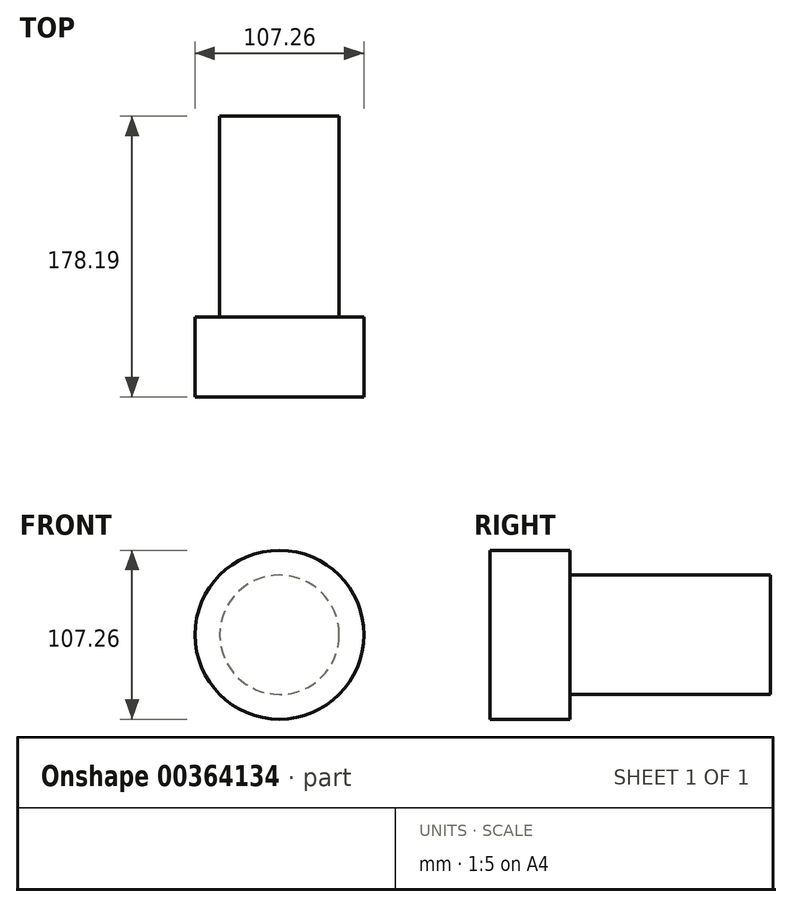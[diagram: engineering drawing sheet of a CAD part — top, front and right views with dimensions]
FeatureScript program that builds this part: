
annotation { "Feature Type Name" : "Feature", "Feature Type Description" : "" }
export const myFeature = defineFeature(function(context is Context, id is Id, definition is map)
    precondition{}
    {
        {
            var Q0;
            Q0=qCreatedBy(makeId("Front.planeOp"),FACE);
            var sketch = newSketch(context, id + "F0", { "sketchPlane" : qUnion([Q0])});
            skCircle(sketch, "E0", {"center": v(0, 0) * mm, "radius": 53.63 * mm});
            skSolve(sketch);
        }
        {
            var Q0;
            Q0 = qSketchRegion(id + "F0", true);
            extrude(context, id + "F1", {"entities" : qUnion([Q0]), "depth" : 50.8 * mm});
        }
        {
            var Q0;
            Q0=qCreatedBy(makeId("Right.planeOp"),FACE);
            var sketch = newSketch(context, id + "F2", { "sketchPlane" : qUnion([Q0])});
            skLineSegment(sketch, "E1.bottom", {"start": v(0, 0) * mm, "end": v(127.4, 0) * mm});
            skLineSegment(sketch, "E1.top", {"start": v(0, 37.9) * mm, "end": v(127.4, 37.9) * mm});
            skLineSegment(sketch, "E1.left", {"start": v(0, 0) * mm, "end": v(0, 37.9) * mm});
            skLineSegment(sketch, "E1.right", {"start": v(127.4, 0) * mm, "end": v(127.4, 37.9) * mm});
            skSolve(sketch);
        }
        {
            var Q0;
            Q0=makeQuery(id+"F2.imprint","IMPRINT",FACE,{"disambiguationData":[TD([[makeQuery(id+"F2.imprint","IMPRINT",EDGE,{"derivedFrom":sQuery(id+"F2.wireOp",EDGE,"E1.bottom")}),1.0]])]});
            var Q1;
            Q1=sQuery(id+"F2.wireOp",EDGE,"E1.bottom");
            revolve(context, id + "F3", {"operationType" : NewBodyOperationType.ADD, "entities" : qUnion([Q0]), "axis" : qUnion([Q1]), "revolveType" : RevolveType.FULL});
        }
    });
